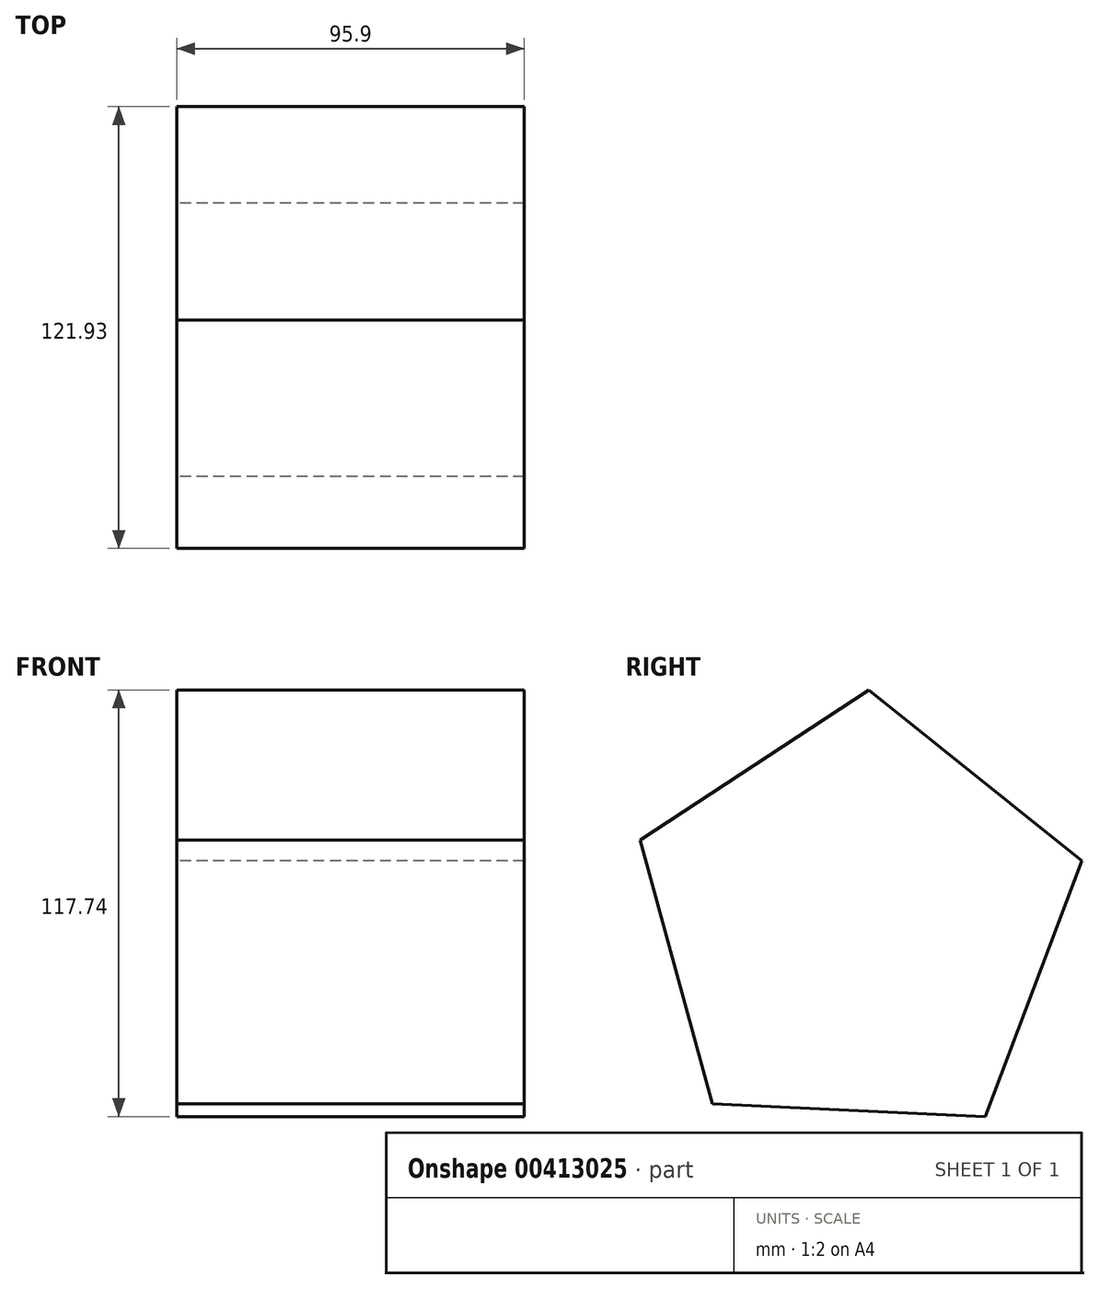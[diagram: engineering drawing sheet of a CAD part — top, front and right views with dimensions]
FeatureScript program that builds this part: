
annotation { "Feature Type Name" : "Feature", "Feature Type Description" : "" }
export const myFeature = defineFeature(function(context is Context, id is Id, definition is map)
    precondition{}
    {
        {
            var Q0;
            Q0=qCreatedBy(makeId("Right.planeOp"),FACE);
            var sketch = newSketch(context, id + "F0", { "sketchPlane" : qUnion([Q0])});
            skCircle(sketch, "E0.cCircle", {"center": v(0, 0) * mm, "radius": 51.92 * mm, "construction": true});
            skLineSegment(sketch, "E0.0", {"start": v(3.04, 64.1) * mm, "end": v(61.9, 16.92) * mm});
            skLineSegment(sketch, "E0.1", {"start": v(61.9, 16.92) * mm, "end": v(35.22, -53.64) * mm});
            skLineSegment(sketch, "E0.2", {"start": v(35.22, -53.64) * mm, "end": v(-40.14, -50.07) * mm});
            skLineSegment(sketch, "E0.3", {"start": v(-40.14, -50.07) * mm, "end": v(-60.03, 22.7) * mm});
            skLineSegment(sketch, "E0.4", {"start": v(-60.03, 22.7) * mm, "end": v(3.04, 64.1) * mm});
            skPoint(sketch, "E0.0.midPoint", {"position": v(32.47, 40.51) * mm});
            skSolve(sketch);
        }
        {
            var Q0;
            Q0 = qSketchRegion(id + "F0", true);
            extrude(context, id + "F1", {"entities" : qUnion([Q0]), "depth" : 95.9 * mm});
        }
    });
